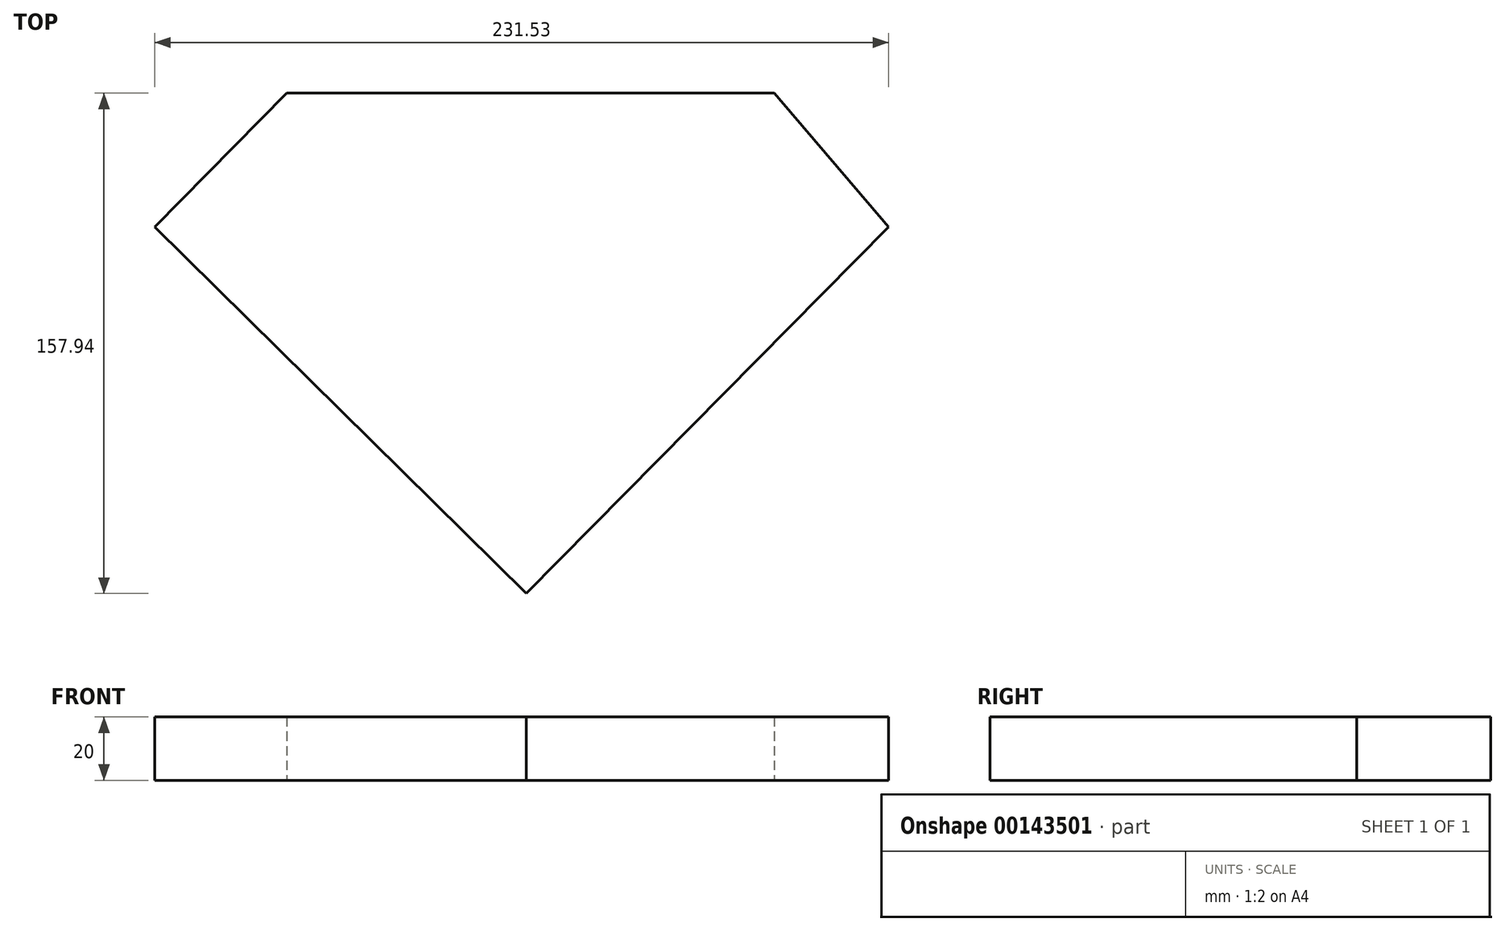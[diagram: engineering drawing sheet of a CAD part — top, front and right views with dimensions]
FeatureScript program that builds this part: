
annotation { "Feature Type Name" : "Feature", "Feature Type Description" : "" }
export const myFeature = defineFeature(function(context is Context, id is Id, definition is map)
    precondition{}
    {
        {
            var Q0;
            Q0=qCreatedBy(makeId("Top.planeOp"),FACE);
            var sketch = newSketch(context, id + "F0", { "sketchPlane" : qUnion([Q0])});
            skLineSegment(sketch, "E0", {"start": v(-78.84, 62.36) * mm, "end": v(74.93, 62.36) * mm});
            skLineSegment(sketch, "E1", {"start": v(-120.53, 20.07) * mm, "end": v(-78.84, 62.36) * mm});
            skLineSegment(sketch, "E2", {"start": v(-120.53, 20.07) * mm, "end": v(-3.29, -95.58) * mm});
            skLineSegment(sketch, "E3", {"start": v(74.93, 62.36) * mm, "end": v(111, 20.07) * mm});
            skLineSegment(sketch, "E4", {"start": v(111, 20.07) * mm, "end": v(-3.29, -95.58) * mm});
            skSolve(sketch);
        }
        {
            var Q0;
            Q0=makeQuery(id+"F0.imprint","IMPRINT",FACE,{"disambiguationData":[TD([[makeQuery(id+"F0.imprint","IMPRINT",EDGE,{"derivedFrom":sQuery(id+"F0.wireOp",EDGE,"E0")}),-1.0]])]});
            extrude(context, id + "F1", {"entities" : qUnion([Q0]), "depth" : 20 * mm});
        }
    });
